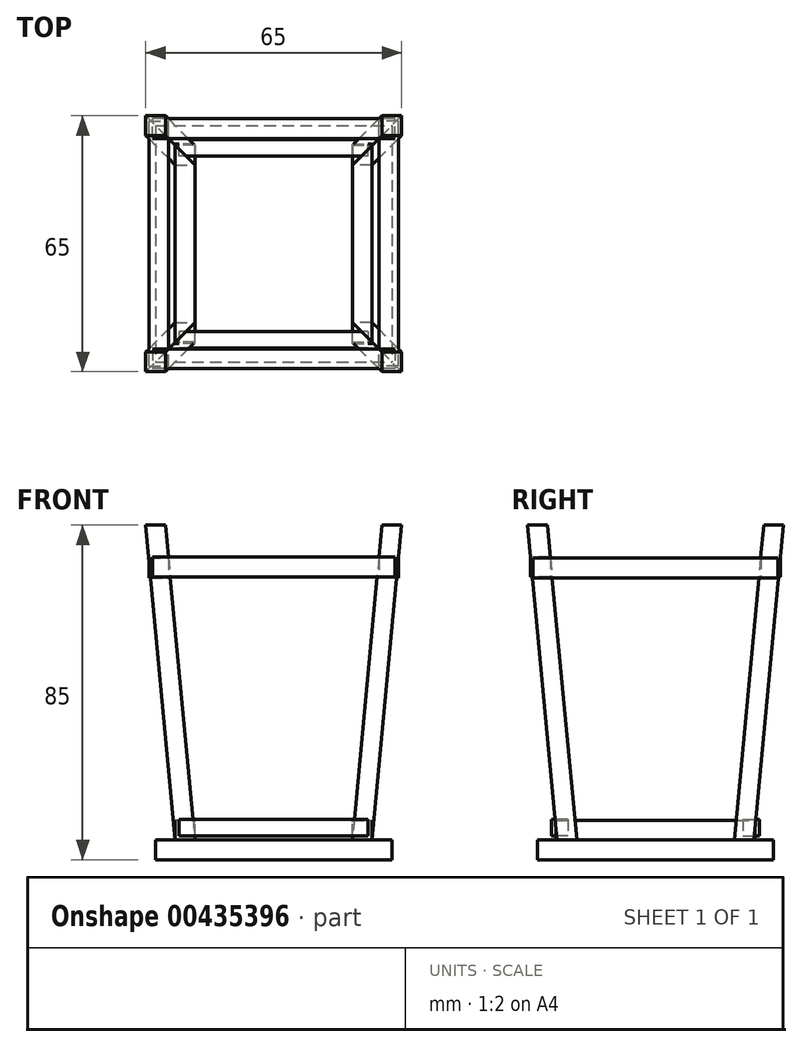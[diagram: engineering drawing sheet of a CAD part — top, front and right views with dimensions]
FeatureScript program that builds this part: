
annotation { "Feature Type Name" : "Feature", "Feature Type Description" : "" }
export const myFeature = defineFeature(function(context is Context, id is Id, definition is map)
    precondition{}
    {
        {
            var Q0;
            Q0=qCreatedBy(makeId("Top.planeOp"),FACE);
            var sketch = newSketch(context, id + "F0", { "sketchPlane" : qUnion([Q0])});
            skLineSegment(sketch, "E0.bottom", {"start": v(25, 25) * mm, "end": v(20, 25) * mm});
            skLineSegment(sketch, "E0.top", {"start": v(25, -25) * mm, "end": v(20, -25) * mm});
            skLineSegment(sketch, "E0.left", {"start": v(25, 25) * mm, "end": v(25, 20) * mm});
            skLineSegment(sketch, "E0.right", {"start": v(-25, 25) * mm, "end": v(-25, 20) * mm});
            skPoint(sketch, "E0.middle", {"position": v(0, 0) * mm});
            skLineSegment(sketch, "E1.top", {"start": v(25, 20) * mm, "end": v(20, 20) * mm});
            skLineSegment(sketch, "E1.right", {"start": v(20, 25) * mm, "end": v(20, 20) * mm});
            skLineSegment(sketch, "E2.MirrorCS", {"start": v(25, -20) * mm, "end": v(20, -20) * mm});
            skLineSegment(sketch, "E3.MirrorCS", {"start": v(20, -25) * mm, "end": v(20, -20) * mm});
            skLineSegment(sketch, "E4.MirrorCS", {"start": v(25, -25) * mm, "end": v(25, -20) * mm});
            skLineSegment(sketch, "E5.MirrorCS", {"start": v(-20, -25) * mm, "end": v(-20, -20) * mm});
            skLineSegment(sketch, "E6.MirrorCS", {"start": v(-25, -20) * mm, "end": v(-20, -20) * mm});
            skLineSegment(sketch, "E7.MirrorCS", {"start": v(-20, 25) * mm, "end": v(-20, 20) * mm});
            skLineSegment(sketch, "E8.MirrorCS", {"start": v(-25, 20) * mm, "end": v(-20, 20) * mm});
            skLineSegment(sketch, "E9.trimOffspring", {"start": v(-20, 25) * mm, "end": v(-25, 25) * mm});
            skLineSegment(sketch, "E10.trimOffspring", {"start": v(-25, -20) * mm, "end": v(-25, -25) * mm});
            skLineSegment(sketch, "E11.trimOffspring", {"start": v(-20, -25) * mm, "end": v(-25, -25) * mm});
            skLineSegment(sketch, "E12.trimOffspring", {"start": v(25, -20) * mm, "end": v(25, -25) * mm});
            skLineSegment(sketch, "E13.bottom", {"start": v(-30, 30) * mm, "end": v(30, 30) * mm});
            skLineSegment(sketch, "E13.top", {"start": v(-30, -30) * mm, "end": v(30, -30) * mm});
            skLineSegment(sketch, "E13.left", {"start": v(-30, 30) * mm, "end": v(-30, -30) * mm});
            skLineSegment(sketch, "E13.right", {"start": v(30, 30) * mm, "end": v(30, -30) * mm});
            skSolve(sketch);
        }
        {
            var Q0;
            Q0=qCreatedBy(makeId("Top.planeOp"),FACE);
            cPlane(context, id + "F1", {"entities" : qUnion([Q0]), "cplaneType" : CPlaneType.OFFSET, "offset" : 80 * mm, "width" : 150 * mm, "height" : 150 * mm});
        }
        {
            var Q0;
            Q0=qCreatedBy(id+"F1.planeOp",FACE);
            var sketch = newSketch(context, id + "F2", { "sketchPlane" : qUnion([Q0])});
            skLineSegment(sketch, "E14.bottom", {"start": v(-32.5, 32.5) * mm, "end": v(-27.5, 32.5) * mm});
            skLineSegment(sketch, "E14.top", {"start": v(-32.5, 27.5) * mm, "end": v(-27.5, 27.5) * mm});
            skLineSegment(sketch, "E14.left", {"start": v(-32.5, 32.5) * mm, "end": v(-32.5, 27.5) * mm});
            skLineSegment(sketch, "E14.right", {"start": v(-27.5, 32.5) * mm, "end": v(-27.5, 27.5) * mm});
            skLineSegment(sketch, "E15.MirrorCS", {"start": v(-32.5, -32.5) * mm, "end": v(-27.5, -32.5) * mm});
            skLineSegment(sketch, "E16.MirrorCS", {"start": v(-32.5, -27.5) * mm, "end": v(-27.5, -27.5) * mm});
            skLineSegment(sketch, "E17.MirrorCS", {"start": v(-32.5, -32.5) * mm, "end": v(-32.5, -27.5) * mm});
            skLineSegment(sketch, "E18.MirrorCS", {"start": v(-27.5, -32.5) * mm, "end": v(-27.5, -27.5) * mm});
            skLineSegment(sketch, "E19.MirrorCS", {"start": v(32.5, 32.5) * mm, "end": v(27.5, 32.5) * mm});
            skLineSegment(sketch, "E20.MirrorCS", {"start": v(32.5, 32.5) * mm, "end": v(32.5, 27.5) * mm});
            skLineSegment(sketch, "E21.MirrorCS", {"start": v(32.5, 27.5) * mm, "end": v(27.5, 27.5) * mm});
            skLineSegment(sketch, "E22.MirrorCS", {"start": v(27.5, 32.5) * mm, "end": v(27.5, 27.5) * mm});
            skLineSegment(sketch, "E23.MirrorCS", {"start": v(32.5, -27.5) * mm, "end": v(27.5, -27.5) * mm});
            skLineSegment(sketch, "E24.MirrorCS", {"start": v(32.5, -32.5) * mm, "end": v(32.5, -27.5) * mm});
            skLineSegment(sketch, "E25.MirrorCS", {"start": v(32.5, -32.5) * mm, "end": v(27.5, -32.5) * mm});
            skLineSegment(sketch, "E26.MirrorCS", {"start": v(27.5, -32.5) * mm, "end": v(27.5, -27.5) * mm});
            skLineSegment(sketch, "E27.trimOffspring", {"start": v(27.5, 32.5) * mm, "end": v(32.5, 32.5) * mm});
            skLineSegment(sketch, "E28.trimOffspring", {"start": v(-32.5, -27.5) * mm, "end": v(-32.5, -32.5) * mm});
            skLineSegment(sketch, "E29.trimOffspring", {"start": v(-27.5, -32.5) * mm, "end": v(-32.5, -32.5) * mm});
            skLineSegment(sketch, "E30.trimOffspring", {"start": v(32.5, -27.5) * mm, "end": v(32.5, -32.5) * mm});
            skSolve(sketch);
        }
        {
            var Q0;
            Q0=makeQuery(id+"F0.imprint","IMPRINT",FACE,{"disambiguationData":[TD([[makeQuery(id+"F0.imprint","IMPRINT",EDGE,{"derivedFrom":sQuery(id+"F0.wireOp",EDGE,"E0.bottom")}),1.0]])]});
            var Q1;
            Q1=makeQuery(id+"F0.imprint","IMPRINT",FACE,{"disambiguationData":[TD([[makeQuery(id+"F0.imprint","IMPRINT",EDGE,{"derivedFrom":sQuery(id+"F0.wireOp",EDGE,"E2.MirrorCS")}),1.0]])]});
            var Q2;
            Q2=makeQuery(id+"F0.imprint","IMPRINT",FACE,{"disambiguationData":[TD([[makeQuery(id+"F0.imprint","IMPRINT",EDGE,{"derivedFrom":sQuery(id+"F0.wireOp",EDGE,"E5.MirrorCS")}),1.0]])]});
            var Q3;
            Q3=makeQuery(id+"F0.imprint","IMPRINT",FACE,{"disambiguationData":[TD([[makeQuery(id+"F0.imprint","IMPRINT",EDGE,{"derivedFrom":sQuery(id+"F0.wireOp",EDGE,"E0.right")}),1.0]])]});
            var Q4;
            Q4=makeQuery(id+"F0.imprint","IMPRINT",FACE,{"disambiguationData":[TD([[makeQuery(id+"F0.imprint","IMPRINT",EDGE,{"derivedFrom":sQuery(id+"F0.wireOp",EDGE,"E0.right")}),-1.0]])]});
            extrude(context, id + "F3", {"entities" : qUnion([Q0, Q1, Q2, Q3, Q4]), "oppositeDirection" : true, "depth" : 5 * mm});
        }
        {
            var Q0;
            Q0=makeQuery(id+"F2.imprint","IMPRINT",FACE,{"disambiguationData":[TD([[makeQuery(id+"F2.imprint","IMPRINT",EDGE,{"derivedFrom":sQuery(id+"F2.wireOp",EDGE,"E16.MirrorCS")}),-1.0]])]});
            var Q1;
            Q1=makeQuery(id+"F0.imprint","IMPRINT",FACE,{"disambiguationData":[TD([[makeQuery(id+"F0.imprint","IMPRINT",EDGE,{"derivedFrom":sQuery(id+"F0.wireOp",EDGE,"E5.MirrorCS")}),1.0]])]});
            loft(context, id + "F4", {"sheetProfilesArray" : [{ "sheetProfileEntities" : qUnion([Q0]) }, { "sheetProfileEntities" : qUnion([Q1]) }]});
        }
        {
            var Q0;
            Q0=makeQuery(id+"F4.opLoft","SWEPT_BODY",BODY,{"disambiguationData":[OSD([makeQuery(id+"F0.imprint","IMPRINT",FACE,{"disambiguationData":[TD([[makeQuery(id+"F0.imprint","IMPRINT",EDGE,{"derivedFrom":sQuery(id+"F0.wireOp",EDGE,"E5.MirrorCS")}),1.0]])]}),makeQuery(id+"F2.imprint","IMPRINT",FACE,{"disambiguationData":[TD([[makeQuery(id+"F2.imprint","IMPRINT",EDGE,{"derivedFrom":sQuery(id+"F2.wireOp",EDGE,"E16.MirrorCS")}),-1.0]])]})])]});
            var Q1;
            Q1=qCreatedBy(makeId("Front.planeOp"),FACE);
            mirror(context, id + "F5", {"entities" : qUnion([Q0]), "mirrorPlane" : qUnion([Q1])});
        }
        {
            var Q0;
            Q0=makeQuery(id+"F5.opPattern","COPY",BODY,{"derivedFrom":makeQuery(id+"F4.opLoft","SWEPT_BODY",BODY,{"disambiguationData":[OSD([makeQuery(id+"F0.imprint","IMPRINT",FACE,{"disambiguationData":[TD([[makeQuery(id+"F0.imprint","IMPRINT",EDGE,{"derivedFrom":sQuery(id+"F0.wireOp",EDGE,"E5.MirrorCS")}),1.0]])]}),makeQuery(id+"F2.imprint","IMPRINT",FACE,{"disambiguationData":[TD([[makeQuery(id+"F2.imprint","IMPRINT",EDGE,{"derivedFrom":sQuery(id+"F2.wireOp",EDGE,"E16.MirrorCS")}),-1.0]])]})])]}),"instanceName":"1"});
            var Q1;
            Q1=makeQuery(id+"F4.opLoft","SWEPT_BODY",BODY,{"disambiguationData":[OSD([makeQuery(id+"F0.imprint","IMPRINT",FACE,{"disambiguationData":[TD([[makeQuery(id+"F0.imprint","IMPRINT",EDGE,{"derivedFrom":sQuery(id+"F0.wireOp",EDGE,"E5.MirrorCS")}),1.0]])]}),makeQuery(id+"F2.imprint","IMPRINT",FACE,{"disambiguationData":[TD([[makeQuery(id+"F2.imprint","IMPRINT",EDGE,{"derivedFrom":sQuery(id+"F2.wireOp",EDGE,"E16.MirrorCS")}),-1.0]])]})])]});
            var Q2;
            Q2=qCreatedBy(makeId("Right.planeOp"),FACE);
            mirror(context, id + "F6", {"entities" : qUnion([Q0, Q1]), "mirrorPlane" : qUnion([Q2])});
        }
        {
            var Q0;
            Q0=qCreatedBy(makeId("Front.planeOp"),FACE);
            var sketch = newSketch(context, id + "F7", { "sketchPlane" : qUnion([Q0])});
            skLineSegment(sketch, "E31.bottom", {"start": v(-20, 0) * mm, "end": v(-25, 0) * mm});
            skLineSegment(sketch, "E31.top", {"start": v(-20, 5) * mm, "end": v(-25, 5) * mm});
            skLineSegment(sketch, "E31.left", {"start": v(-20, 0) * mm, "end": v(-20, 5) * mm});
            skLineSegment(sketch, "E31.right", {"start": v(-25, 0) * mm, "end": v(-25, 5) * mm});
            skPoint(sketch, "E31.middle", {"position": v(-22.5, 2.5) * mm});
            skSolve(sketch);
        }
        {
            var Q0;
            Q0 = qSketchRegion(id + "F7", true);
            extrude(context, id + "F8", {"entities" : qUnion([Q0]), "endBound" : BoundingType.SYMMETRIC, "depth" : 50.6 * mm});
        }
        {
            var Q0;
            Q0=makeQuery(id+"F8.opExtrude","SWEPT_BODY",BODY,{"disambiguationData":[OSD([sQuery(id+"F7.wireOp",EDGE,"E31.bottom"),sQuery(id+"F7.wireOp",EDGE,"E31.top"),sQuery(id+"F7.wireOp",EDGE,"E31.left"),sQuery(id+"F7.wireOp",EDGE,"E31.right")])]});
            var Q1;
            Q1=qCreatedBy(makeId("Right.planeOp"),FACE);
            mirror(context, id + "F9", {"entities" : qUnion([Q0]), "mirrorPlane" : qUnion([Q1])});
        }
        {
            var Q0;
            Q0=qCreatedBy(makeId("Right.planeOp"),FACE);
            var sketch = newSketch(context, id + "F10", { "sketchPlane" : qUnion([Q0])});
            skLineSegment(sketch, "E32.bottom", {"start": v(-26.74, 71.86) * mm, "end": v(-31.74, 71.86) * mm});
            skLineSegment(sketch, "E32.top", {"start": v(-26.74, 66.86) * mm, "end": v(-31.74, 66.86) * mm});
            skLineSegment(sketch, "E32.left", {"start": v(-26.74, 71.86) * mm, "end": v(-26.74, 66.86) * mm});
            skLineSegment(sketch, "E32.right", {"start": v(-31.74, 71.86) * mm, "end": v(-31.74, 66.86) * mm});
            skPoint(sketch, "E32.middle", {"position": v(-29.24, 69.36) * mm});
            skLineSegment(sketch, "E33.MirrorCS", {"start": v(26.74, 71.86) * mm, "end": v(31.74, 71.86) * mm});
            skLineSegment(sketch, "E34.MirrorCS", {"start": v(31.74, 71.86) * mm, "end": v(31.74, 66.86) * mm});
            skLineSegment(sketch, "E35.MirrorCS", {"start": v(26.74, 66.86) * mm, "end": v(31.74, 66.86) * mm});
            skLineSegment(sketch, "E36.MirrorCS", {"start": v(26.74, 71.86) * mm, "end": v(26.74, 66.86) * mm});
            skLineSegment(sketch, "E37.bottom", {"start": v(-22.26, 5.26) * mm, "end": v(-26.46, 5.26) * mm});
            skLineSegment(sketch, "E37.top", {"start": v(-22.26, 1.1) * mm, "end": v(-26.46, 1.1) * mm});
            skLineSegment(sketch, "E37.left", {"start": v(-22.26, 5.26) * mm, "end": v(-22.26, 1.1) * mm});
            skLineSegment(sketch, "E37.right", {"start": v(-26.46, 5.26) * mm, "end": v(-26.46, 1.1) * mm});
            skPoint(sketch, "E37.middle", {"position": v(-24.36, 3.18) * mm});
            skSolve(sketch);
        }
        {
            var Q0;
            Q0=makeQuery(id+"F10.imprint","IMPRINT",FACE,{"disambiguationData":[TD([[makeQuery(id+"F10.imprint","IMPRINT",EDGE,{"derivedFrom":sQuery(id+"F10.wireOp",EDGE,"E32.bottom")}),1.0]])]});
            extrude(context, id + "F11", {"entities" : qUnion([Q0]), "endBound" : BoundingType.SYMMETRIC, "depth" : 61.6 * mm});
        }
        {
            var Q0;
            Q0=makeQuery(id+"F11.opExtrude","SWEPT_BODY",BODY,{"disambiguationData":[OSD([sQuery(id+"F10.wireOp",EDGE,"E32.bottom"),sQuery(id+"F10.wireOp",EDGE,"E32.top"),sQuery(id+"F10.wireOp",EDGE,"E32.left"),sQuery(id+"F10.wireOp",EDGE,"E32.right")])]});
            var Q1;
            Q1=qCreatedBy(makeId("Front.planeOp"),FACE);
            mirror(context, id + "F12", {"entities" : qUnion([Q0]), "mirrorPlane" : qUnion([Q1])});
        }
        {
            var Q0;
            Q0=makeQuery(id+"F10.imprint","IMPRINT",FACE,{"disambiguationData":[TD([[makeQuery(id+"F10.imprint","IMPRINT",EDGE,{"derivedFrom":sQuery(id+"F10.wireOp",EDGE,"E37.bottom")}),1.0]])]});
            extrude(context, id + "F13", {"entities" : qUnion([Q0]), "endBound" : BoundingType.SYMMETRIC, "depth" : 48 * mm});
        }
        {
            var Q0;
            Q0=makeQuery(id+"F13.opExtrude","SWEPT_BODY",BODY,{"disambiguationData":[OSD([sQuery(id+"F10.wireOp",EDGE,"E37.bottom"),sQuery(id+"F10.wireOp",EDGE,"E37.top"),sQuery(id+"F10.wireOp",EDGE,"E37.left"),sQuery(id+"F10.wireOp",EDGE,"E37.right")])]});
            var Q1;
            Q1=qCreatedBy(makeId("Front.planeOp"),FACE);
            mirror(context, id + "F14", {"entities" : qUnion([Q0]), "mirrorPlane" : qUnion([Q1])});
        }
        {
            var Q0;
            Q0=qCreatedBy(makeId("Front.planeOp"),FACE);
            var sketch = newSketch(context, id + "F15", { "sketchPlane" : qUnion([Q0])});
            skLineSegment(sketch, "E38.bottom", {"start": v(-31.72, 71.63) * mm, "end": v(-26.72, 71.63) * mm});
            skLineSegment(sketch, "E38.top", {"start": v(-31.72, 66.63) * mm, "end": v(-26.72, 66.63) * mm});
            skLineSegment(sketch, "E38.left", {"start": v(-31.72, 71.63) * mm, "end": v(-31.72, 66.63) * mm});
            skLineSegment(sketch, "E38.right", {"start": v(-26.72, 71.63) * mm, "end": v(-26.72, 66.63) * mm});
            skLineSegment(sketch, "E39.MirrorCS", {"start": v(26.72, 71.63) * mm, "end": v(26.72, 66.63) * mm});
            skLineSegment(sketch, "E40.MirrorCS", {"start": v(31.72, 71.63) * mm, "end": v(26.72, 71.63) * mm});
            skLineSegment(sketch, "E41.MirrorCS", {"start": v(31.72, 71.63) * mm, "end": v(31.72, 66.63) * mm});
            skLineSegment(sketch, "E42.MirrorCS", {"start": v(31.72, 66.63) * mm, "end": v(26.72, 66.63) * mm});
            skSolve(sketch);
        }
        {
            var Q0;
            Q0=makeQuery(id+"F15.imprint","IMPRINT",FACE,{"disambiguationData":[TD([[makeQuery(id+"F15.imprint","IMPRINT",EDGE,{"derivedFrom":sQuery(id+"F15.wireOp",EDGE,"E38.bottom")}),-1.0]])]});
            extrude(context, id + "F16", {"entities" : qUnion([Q0]), "endBound" : BoundingType.SYMMETRIC, "depth" : 62.2 * mm});
        }
        {
            var Q0;
            Q0=makeQuery(id+"F16.opExtrude","SWEPT_BODY",BODY,{"disambiguationData":[OSD([sQuery(id+"F15.wireOp",EDGE,"E38.bottom"),sQuery(id+"F15.wireOp",EDGE,"E38.top"),sQuery(id+"F15.wireOp",EDGE,"E38.left"),sQuery(id+"F15.wireOp",EDGE,"E38.right")])]});
            var Q1;
            Q1=qCreatedBy(makeId("Right.planeOp"),FACE);
            mirror(context, id + "F17", {"entities" : qUnion([Q0]), "mirrorPlane" : qUnion([Q1])});
        }
    });
